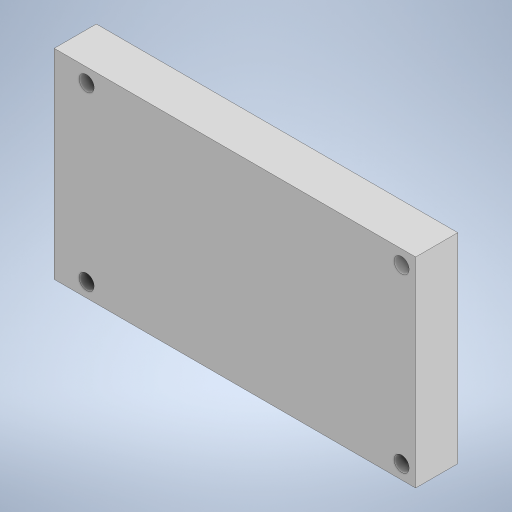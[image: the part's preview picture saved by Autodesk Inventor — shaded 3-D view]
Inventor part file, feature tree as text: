
AUTODESK INVENTOR PART (.ipt)
format: ipt  version: 2023 (Build 270158000, 158)  size: 195,072 bytes
history: native  units: in
note: dims shown in document units (in); Inventor stores cm internally (conversion verified against a paired STEP export)
features: extrude x1, other x1
ambient origin geometry x8: Origin, YZ Plane, XZ Plane, XY Plane, X Axis, Y Axis, Z Axis, Center Point
bodies: Solid1 (feature_tree)
feature tree (2):
  extrude  "Extrusion1"  Depth=0.1181in
  other  "Ecran"
